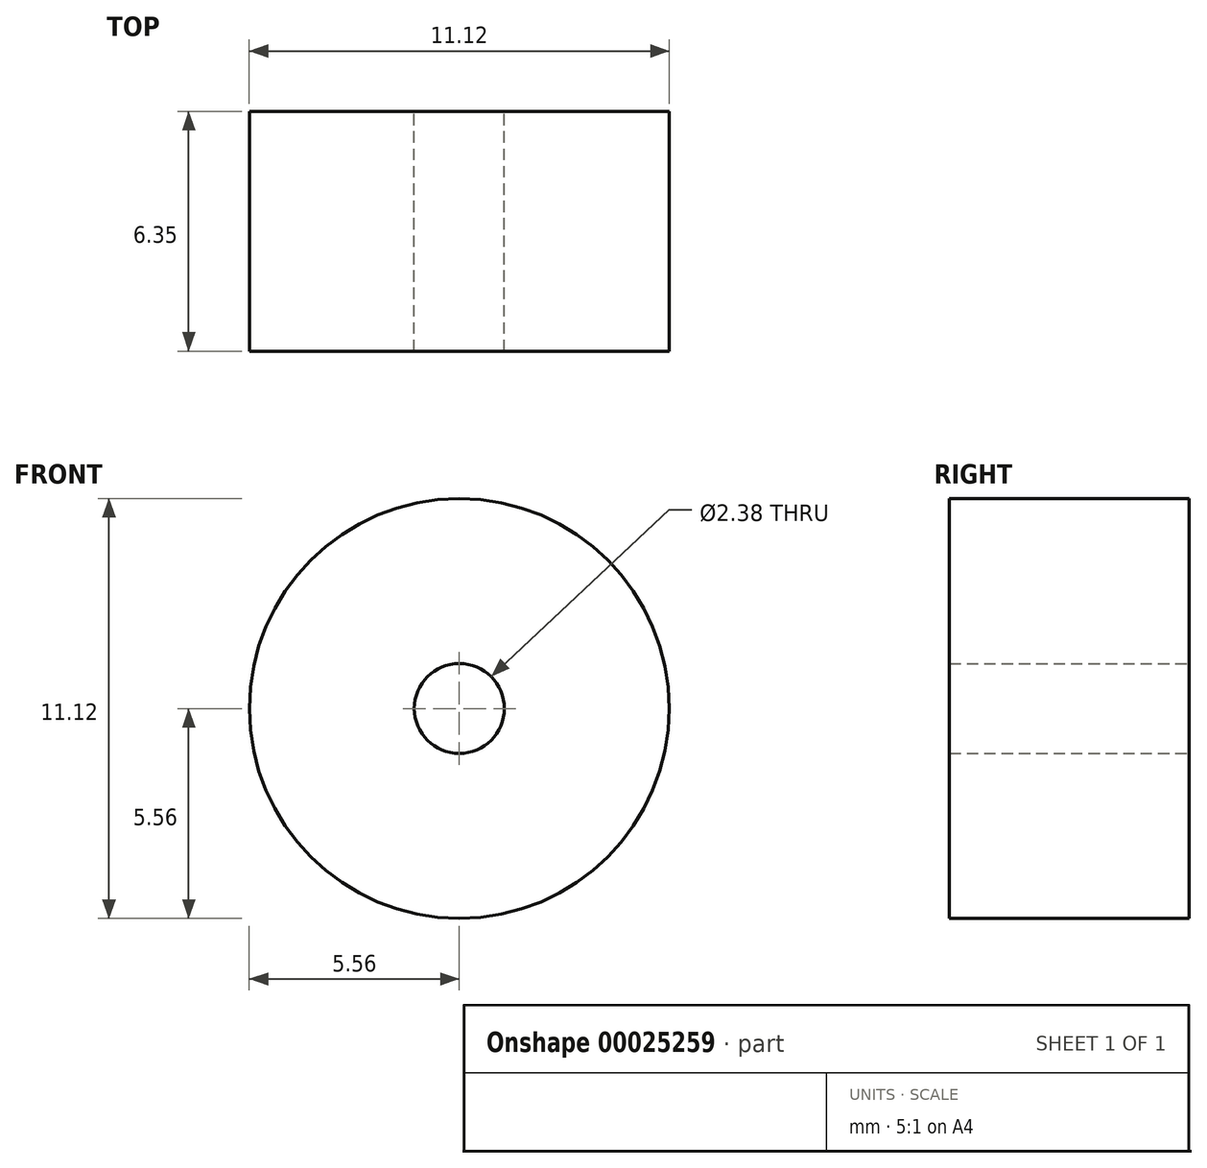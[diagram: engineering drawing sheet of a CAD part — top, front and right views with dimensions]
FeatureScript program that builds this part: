
annotation { "Feature Type Name" : "Feature", "Feature Type Description" : "" }
export const myFeature = defineFeature(function(context is Context, id is Id, definition is map)
    precondition{}
    {
        {
            var Q0;
            Q0=qCreatedBy(makeId("Front.planeOp"),FACE);
            var sketch = newSketch(context, id + "F0", { "sketchPlane" : qUnion([Q0])});
            skCircle(sketch, "E0", {"center": v(0, 0) * mm, "radius": 5.56 * mm});
            skCircle(sketch, "E1", {"center": v(0, 0) * mm, "radius": 1.2 * mm});
            skSolve(sketch);
        }
        {
            var Q0;
            Q0=makeQuery(id+"F0.imprint","IMPRINT",FACE,{"disambiguationData":[TD([[makeQuery(id+"F0.imprint","IMPRINT",EDGE,{"derivedFrom":sQuery(id+"F0.wireOp",EDGE,"E0")}),1.0]])]});
            extrude(context, id + "F1", {"entities" : qUnion([Q0]), "depth" : 6.35 * mm});
        }
    });
